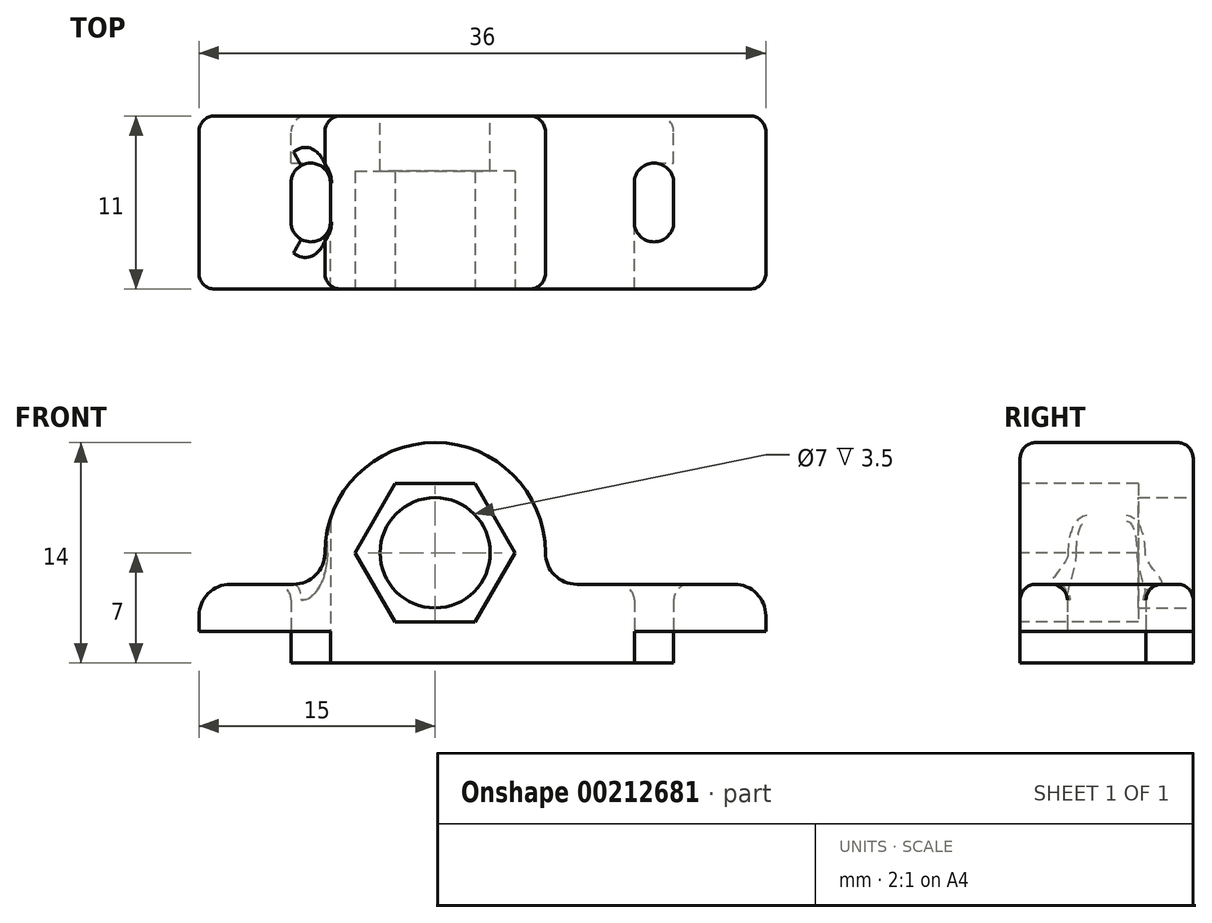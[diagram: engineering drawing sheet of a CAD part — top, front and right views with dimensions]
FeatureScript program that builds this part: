
annotation { "Feature Type Name" : "Feature", "Feature Type Description" : "" }
export const myFeature = defineFeature(function(context is Context, id is Id, definition is map)
    precondition{}
    {
        {
            var Q0;
            Q0=qCreatedBy(makeId("Front.planeOp"),FACE);
            var sketch = newSketch(context, id + "F0", { "sketchPlane" : qUnion([Q0])});
            skLineSegment(sketch, "E0.top", {"start": v(-12.15, -2) * mm, "end": v(12.15, -2) * mm});
            skLineSegment(sketch, "E0.left", {"start": v(-12.15, 0) * mm, "end": v(-12.15, -2) * mm});
            skLineSegment(sketch, "E0.right", {"start": v(12.15, 0) * mm, "end": v(12.15, -2) * mm});
            skLineSegment(sketch, "E1.bottom", {"start": v(-16, 3) * mm, "end": v(-12, 3) * mm});
            skLineSegment(sketch, "E1.top", {"start": v(-18, 0) * mm, "end": v(-12.15, 0) * mm});
            skLineSegment(sketch, "E1.left", {"start": v(-18, 1) * mm, "end": v(-18, 0) * mm});
            skLineSegment(sketch, "E1.right", {"start": v(18, 1) * mm, "end": v(18, 0) * mm});
            skLineSegment(sketch, "E2.trimOffspring", {"start": v(12.15, 0) * mm, "end": v(18, 0) * mm});
            skLineSegment(sketch, "E3.top", {"start": v(-3, 12) * mm, "end": v(-3, 12) * mm});
            skLineSegment(sketch, "E3.left", {"start": v(-10, 5) * mm, "end": v(-10, 5) * mm});
            skLineSegment(sketch, "E3.right", {"start": v(4, 5) * mm, "end": v(4, 5) * mm});
            skLineSegment(sketch, "E4", {"start": v(-3, 12) * mm, "end": v(-3, 3) * mm, "construction": true});
            skLineSegment(sketch, "E5.trimOffspring", {"start": v(6, 3) * mm, "end": v(16, 3) * mm});
            skCircle(sketch, "E6", {"center": v(-3, 5) * mm, "radius": 3.5 * mm});
            skPoint(sketch, "E7.visualSharp", {"position": v(-10, 12) * mm});
            skArc(sketch, "E7.filletArc", {"start": v(-3, 12) * mm, "mid": v(-7.95, 9.95) * mm, "end": v(-10, 5) * mm});
            skPoint(sketch, "E8.visualSharp", {"position": v(4, 12) * mm});
            skArc(sketch, "E8.filletArc", {"start": v(4, 5) * mm, "mid": v(1.95, 9.95) * mm, "end": v(-3, 12) * mm});
            skPoint(sketch, "E9.visualSharp", {"position": v(-10, 3) * mm});
            skArc(sketch, "E9.filletArc", {"start": v(-12, 3) * mm, "mid": v(-10.59, 3.59) * mm, "end": v(-10, 5) * mm});
            skPoint(sketch, "E10.visualSharp", {"position": v(4, 3) * mm});
            skArc(sketch, "E10.filletArc", {"start": v(4, 5) * mm, "mid": v(4.59, 3.59) * mm, "end": v(6, 3) * mm});
            skPoint(sketch, "E11.visualSharp", {"position": v(-18, 3) * mm});
            skArc(sketch, "E11.filletArc", {"start": v(-16, 3) * mm, "mid": v(-17.41, 2.41) * mm, "end": v(-18, 1) * mm});
            skPoint(sketch, "E12.visualSharp", {"position": v(18, 3) * mm});
            skArc(sketch, "E12.filletArc", {"start": v(18, 1) * mm, "mid": v(17.41, 2.41) * mm, "end": v(16, 3) * mm});
            skSolve(sketch);
        }
        {
            var Q0;
            Q0 = qSketchRegion(id + "F0", true);
            extrude(context, id + "F1", {"entities" : qUnion([Q0]), "depth" : 11 * mm});
        }
        {
            var Q0;
            Q0=makeQuery(id+"F1.opExtrude","CAP_FACE",FACE,{"disambiguationData":[OSD([sQuery(id+"F0.wireOp",EDGE,"E0.top"),sQuery(id+"F0.wireOp",EDGE,"E0.left"),sQuery(id+"F0.wireOp",EDGE,"E0.right"),sQuery(id+"F0.wireOp",EDGE,"E1.bottom"),sQuery(id+"F0.wireOp",EDGE,"E1.top"),sQuery(id+"F0.wireOp",EDGE,"E1.left"),sQuery(id+"F0.wireOp",EDGE,"E1.right"),sQuery(id+"F0.wireOp",EDGE,"E2.trimOffspring"),sQuery(id+"F0.wireOp",EDGE,"E5.trimOffspring"),sQuery(id+"F0.wireOp",EDGE,"E6"),sQuery(id+"F0.wireOp",EDGE,"E7.filletArc"),sQuery(id+"F0.wireOp",EDGE,"E8.filletArc"),sQuery(id+"F0.wireOp",EDGE,"E9.filletArc"),sQuery(id+"F0.wireOp",EDGE,"E10.filletArc"),sQuery(id+"F0.wireOp",EDGE,"E11.filletArc"),sQuery(id+"F0.wireOp",EDGE,"E12.filletArc")])],"isStart":false});
            var sketch = newSketch(context, id + "F2", { "sketchPlane" : qUnion([Q0])});
            skCircle(sketch, "E13.cCircle", {"center": v(-3, 5) * mm, "radius": 4.4 * mm, "construction": true});
            skLineSegment(sketch, "E13.0", {"start": v(-0.46, 0.6) * mm, "end": v(-5.54, 0.6) * mm});
            skLineSegment(sketch, "E13.1", {"start": v(-5.54, 0.6) * mm, "end": v(-8.08, 5) * mm});
            skLineSegment(sketch, "E13.2", {"start": v(-8.08, 5) * mm, "end": v(-5.54, 9.4) * mm});
            skLineSegment(sketch, "E13.3", {"start": v(-5.54, 9.4) * mm, "end": v(-0.46, 9.4) * mm});
            skLineSegment(sketch, "E13.4", {"start": v(-0.46, 9.4) * mm, "end": v(2.08, 5) * mm});
            skLineSegment(sketch, "E13.5", {"start": v(2.08, 5) * mm, "end": v(-0.46, 0.6) * mm});
            skPoint(sketch, "E13.0.midPoint", {"position": v(-3, 0.6) * mm});
            skSolve(sketch);
        }
        {
            var Q0;
            Q0 = qSketchRegion(id + "F2", true);
            extrude(context, id + "F3", {"entities" : qUnion([Q0]), "operationType" : NewBodyOperationType.REMOVE, "oppositeDirection" : true, "depth" : 7.5 * mm});
        }
        {
            var Q0;
            Q0=makeQuery(id+"F1.opExtrude","SWEPT_FACE",FACE,{"disambiguationData":[OSD([sQuery(id+"F0.wireOp",EDGE,"E0.top")])]});
            var sketch = newSketch(context, id + "F4", { "sketchPlane" : qUnion([Q0])});
            skLineSegment(sketch, "E14.bottom", {"start": v(-12.15, 6.75) * mm, "end": v(-9.65, 6.75) * mm, "construction": true});
            skLineSegment(sketch, "E14.top", {"start": v(-12.15, 4.25) * mm, "end": v(-9.65, 4.25) * mm, "construction": true});
            skLineSegment(sketch, "E14.left", {"start": v(-12.15, 6.75) * mm, "end": v(-12.15, 4.25) * mm});
            skLineSegment(sketch, "E14.right", {"start": v(-9.65, 6.75) * mm, "end": v(-9.65, 4.25) * mm});
            skLineSegment(sketch, "E15.bottom", {"start": v(12.15, 6.75) * mm, "end": v(9.65, 6.75) * mm, "construction": true});
            skLineSegment(sketch, "E15.top", {"start": v(12.15, 4.25) * mm, "end": v(9.65, 4.25) * mm, "construction": true});
            skLineSegment(sketch, "E15.left", {"start": v(12.15, 6.75) * mm, "end": v(12.15, 4.25) * mm});
            skLineSegment(sketch, "E15.right", {"start": v(9.65, 6.75) * mm, "end": v(9.65, 4.25) * mm});
            skArc(sketch, "E16", {"start": v(-9.65, 6.75) * mm, "mid": v(-10.9, 8) * mm, "end": v(-12.15, 6.75) * mm});
            skArc(sketch, "E17", {"start": v(-12.15, 4.25) * mm, "mid": v(-10.9, 3) * mm, "end": v(-9.65, 4.25) * mm});
            skArc(sketch, "E18", {"start": v(12.15, 6.75) * mm, "mid": v(10.9, 8) * mm, "end": v(9.65, 6.75) * mm});
            skArc(sketch, "E19", {"start": v(9.65, 4.25) * mm, "mid": v(10.9, 3) * mm, "end": v(12.15, 4.25) * mm});
            skSolve(sketch);
        }
        {
            var Q0;
            Q0 = qSketchRegion(id + "F4", true);
            extrude(context, id + "F5", {"entities" : qUnion([Q0]), "operationType" : NewBodyOperationType.REMOVE, "endBound" : BoundingType.THROUGH_ALL, "oppositeDirection" : true, "depth" : 25 * mm});
        }
        {
            var Q0;
            Q0=makeQuery(id+"F1.opExtrude","SWEPT_FACE",FACE,{"disambiguationData":[OSD([sQuery(id+"F0.wireOp",EDGE,"E0.top")])]});
            var sketch = newSketch(context, id + "F6", { "sketchPlane" : qUnion([Q0])});
            skLineSegment(sketch, "E20.top", {"start": v(-12.15, 3) * mm, "end": v(-10.9, 3) * mm});
            skLineSegment(sketch, "E20.left", {"start": v(-12.15, 6.75) * mm, "end": v(-12.15, 3) * mm});
            skLineSegment(sketch, "E20.right", {"start": v(-10.9, 6.75) * mm, "end": v(-10.9, 3) * mm});
            skLineSegment(sketch, "E21.top", {"start": v(10.9, 3) * mm, "end": v(12.15, 3) * mm});
            skLineSegment(sketch, "E21.left", {"start": v(10.9, 6.75) * mm, "end": v(10.9, 3) * mm});
            skLineSegment(sketch, "E22.bottom", {"start": v(-12.15, 11) * mm, "end": v(-9.65, 11) * mm});
            skLineSegment(sketch, "E22.top", {"start": v(-10.9, 6.75) * mm, "end": v(-9.65, 6.75) * mm});
            skLineSegment(sketch, "E22.left", {"start": v(-12.15, 11) * mm, "end": v(-12.15, 6.75) * mm});
            skLineSegment(sketch, "E22.right", {"start": v(-9.65, 11) * mm, "end": v(-9.65, 6.75) * mm});
            skLineSegment(sketch, "E23.bottom", {"start": v(12.15, 11) * mm, "end": v(9.65, 11) * mm});
            skLineSegment(sketch, "E23.top", {"start": v(10.9, 6.75) * mm, "end": v(9.65, 6.75) * mm});
            skLineSegment(sketch, "E23.right", {"start": v(9.65, 11) * mm, "end": v(9.65, 6.75) * mm});
            skLineSegment(sketch, "E24", {"start": v(12.15, 11) * mm, "end": v(12.15, 3) * mm});
            skSolve(sketch);
        }
        {
            var Q0;
            Q0 = qSketchRegion(id + "F6", true);
            extrude(context, id + "F7", {"entities" : qUnion([Q0]), "operationType" : NewBodyOperationType.REMOVE, "oppositeDirection" : true, "depth" : 2 * mm});
        }
        {
            var Q0;
            Q0=makeQuery(id+"F1.opExtrude","CAP_EDGE",EDGE,{"disambiguationData":[OSD([sQuery(id+"F0.wireOp",EDGE,"E0.left")])],"isStart":true});
            var Q1;
            Q1=makeQuery(id+"F1.opExtrude","CAP_EDGE",EDGE,{"disambiguationData":[OSD([sQuery(id+"F0.wireOp",EDGE,"E0.right")])],"isStart":true});
            var Q2;
            Q2=makeQuery(id+"F1.opExtrude","CAP_EDGE",EDGE,{"disambiguationData":[OSD([sQuery(id+"F0.wireOp",EDGE,"E0.right")])],"isStart":false});
            var Q3;
            Q3=makeQuery(id+"F1.opExtrude","CAP_EDGE",EDGE,{"disambiguationData":[OSD([sQuery(id+"F0.wireOp",EDGE,"E0.left")])],"isStart":false});
            fillet(context, id + "F8", {"entities" : qUnion([Q0, Q1, Q2, Q3]), "radius" : 1 * mm, "tangentPropagation" : true, "allowEdgeOverflow" : false});
        }
        {
            var Q0;
            Q0=makeQuery(id+"F1.opExtrude","CAP_EDGE",EDGE,{"disambiguationData":[OSD([sQuery(id+"F0.wireOp",EDGE,"E11.filletArc")])],"isStart":true});
            var Q1;
            Q1=makeQuery(id+"F1.opExtrude","CAP_EDGE",EDGE,{"disambiguationData":[OSD([sQuery(id+"F0.wireOp",EDGE,"E11.filletArc")])],"isStart":false});
            var Q2;
            Q2=makeQuery(id+"F5.boolean.opBoolean","INTERSECT",EDGE,{"derivedFrom":[makeQuery(id+"F1.opExtrude","SWEPT_FACE",FACE,{"disambiguationData":[OSD([sQuery(id+"F0.wireOp",EDGE,"E5.trimOffspring")])]}),makeQuery(id+"F5.opExtrude","SWEPT_FACE",FACE,{"disambiguationData":[OSD([sQuery(id+"F4.wireOp",EDGE,"E15.left")])]})]});
            var Q3;
            Q3=makeQuery(id+"F5.boolean.opBoolean","INTERSECT",EDGE,{"derivedFrom":[makeQuery(id+"F1.opExtrude","SWEPT_FACE",FACE,{"disambiguationData":[OSD([sQuery(id+"F0.wireOp",EDGE,"E1.bottom")])]}),makeQuery(id+"F5.opExtrude","SWEPT_FACE",FACE,{"disambiguationData":[OSD([sQuery(id+"F4.wireOp",EDGE,"E14.left")])]})]});
            fillet(context, id + "F9", {"entities" : qUnion([Q0, Q1, Q2, Q3]), "radius" : 1 * mm, "tangentPropagation" : true, "allowEdgeOverflow" : false});
        }
    });
